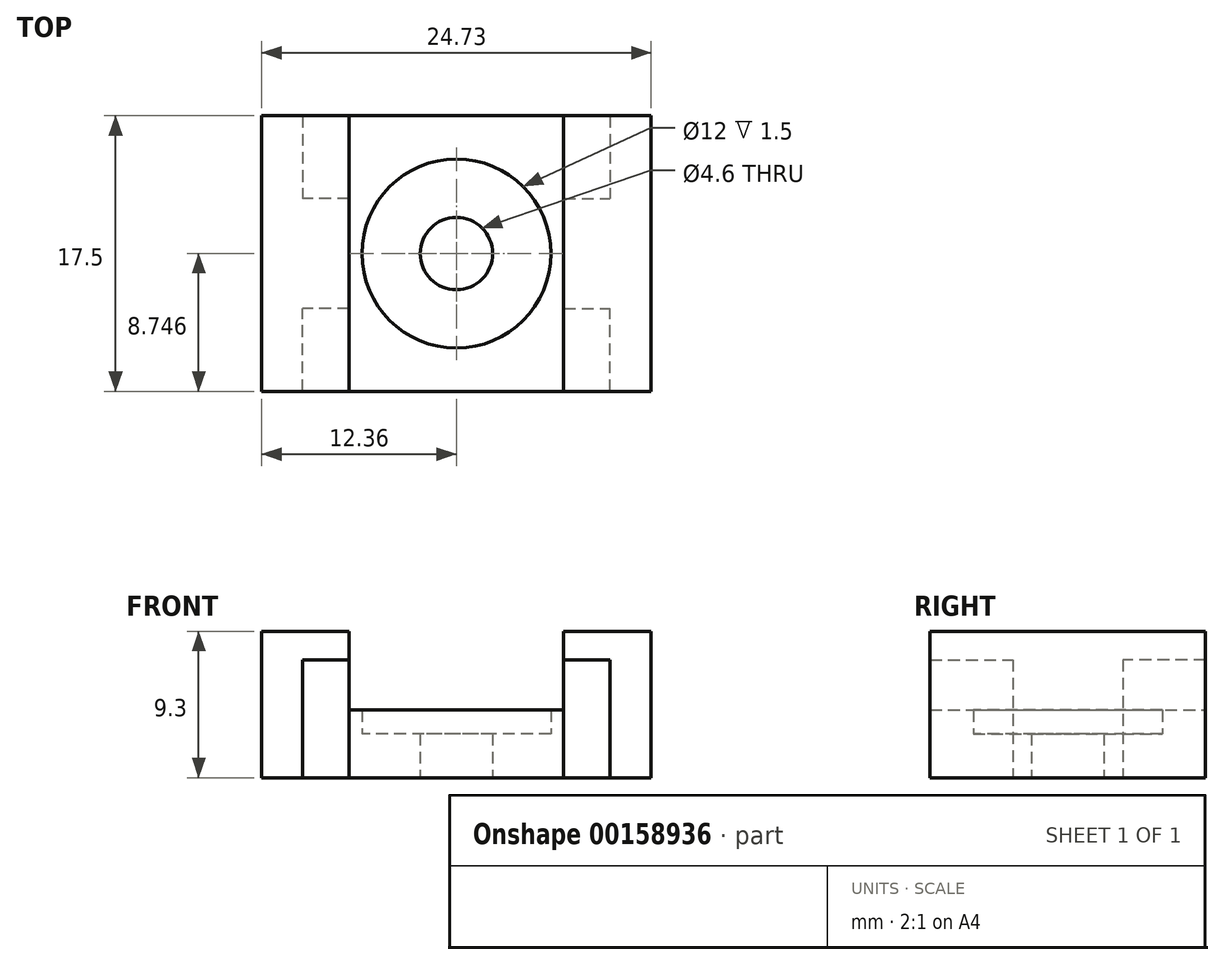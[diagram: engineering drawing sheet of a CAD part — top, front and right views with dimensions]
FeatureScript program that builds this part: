
annotation { "Feature Type Name" : "Feature", "Feature Type Description" : "" }
export const myFeature = defineFeature(function(context is Context, id is Id, definition is map)
    precondition{}
    {
        {
            var Q0;
            Q0=qCreatedBy(makeId("Top.planeOp"),FACE);
            var sketch = newSketch(context, id + "F0", { "sketchPlane" : qUnion([Q0])});
            skLineSegment(sketch, "E0.bottom", {"start": v(11.49, -0.86) * mm, "end": v(36.22, -0.86) * mm});
            skLineSegment(sketch, "E0.top", {"start": v(11.49, -18.36) * mm, "end": v(36.22, -18.36) * mm});
            skLineSegment(sketch, "E0.left", {"start": v(11.49, -0.86) * mm, "end": v(11.49, -18.36) * mm});
            skLineSegment(sketch, "E0.right", {"start": v(36.22, -0.86) * mm, "end": v(36.22, -18.36) * mm});
            skLineSegment(sketch, "E1", {"start": v(11.49, -18.36) * mm, "end": v(17.04, -18.36) * mm, "construction": true});
            skLineSegment(sketch, "E2", {"start": v(36.22, -18.36) * mm, "end": v(30.67, -18.36) * mm, "construction": true});
            skLineSegment(sketch, "E3", {"start": v(30.67, -18.36) * mm, "end": v(30.67, -0.86) * mm});
            skLineSegment(sketch, "E4", {"start": v(17.04, -18.36) * mm, "end": v(17.04, -0.86) * mm});
            skLineSegment(sketch, "E5", {"start": v(11.49, -9.61) * mm, "end": v(36.22, -9.61) * mm, "construction": true});
            skLineSegment(sketch, "E6", {"start": v(23.85, -0.86) * mm, "end": v(23.85, -18.36) * mm, "construction": true});
            skLineSegment(sketch, "E7", {"start": v(11.49, -13.1) * mm, "end": v(14.09, -13.1) * mm, "construction": true});
            skLineSegment(sketch, "E8", {"start": v(14.09, -13.1) * mm, "end": v(14.09, -18.36) * mm});
            skLineSegment(sketch, "E9", {"start": v(14.09, -13.1) * mm, "end": v(17.04, -13.1) * mm});
            skLineSegment(sketch, "E10.MirrorCS", {"start": v(33.62, -13.1) * mm, "end": v(30.67, -13.1) * mm});
            skLineSegment(sketch, "E11.MirrorCS", {"start": v(33.62, -13.1) * mm, "end": v(33.62, -18.36) * mm});
            skLineSegment(sketch, "E12.MirrorCS", {"start": v(33.62, -6.12) * mm, "end": v(30.67, -6.12) * mm});
            skLineSegment(sketch, "E13.MirrorCS", {"start": v(33.62, -6.12) * mm, "end": v(33.62, -0.86) * mm});
            skLineSegment(sketch, "E14.MirrorCS", {"start": v(14.09, -6.12) * mm, "end": v(17.04, -6.12) * mm});
            skLineSegment(sketch, "E15.MirrorCS", {"start": v(14.09, -6.12) * mm, "end": v(14.09, -0.86) * mm});
            skCircle(sketch, "E16", {"center": v(23.85, -9.61) * mm, "radius": 6 * mm});
            skCircle(sketch, "E17", {"center": v(23.85, -9.61) * mm, "radius": 2.3 * mm});
            skSolve(sketch);
        }
        {
            var Q0;
            {var subQ3=sQuery(id+"F0.wireOp",EDGE,"E0.right");Q0=makeQuery(id+"F0.imprint","IMPRINT",FACE,{"disambiguationData":[TD([[makeQuery(id+"F0.imprint","IMPRINT",EDGE,{"derivedFrom":subQ3}),-1.0]])]});}
            var Q1;
            {var subQ0=sQuery(id+"F0.wireOp",EDGE,"E0.left");Q1=makeQuery(id+"F0.imprint","IMPRINT",FACE,{"disambiguationData":[TD([[makeQuery(id+"F0.imprint","IMPRINT",EDGE,{"derivedFrom":subQ0}),1.0]])]});}
            extrude(context, id + "F1", {"entities" : qUnion([Q0, Q1]), "depth" : 9.3 * mm});
        }
        {
            var Q0;
            Q0=makeQuery(id+"F0.imprint","IMPRINT",FACE,{"disambiguationData":[TD([[makeQuery(id+"F0.imprint","IMPRINT",EDGE,{"derivedFrom":sQuery(id+"F0.wireOp",EDGE,"E16")}),-1.0]])]});
            extrude(context, id + "F2", {"entities" : qUnion([Q0]), "depth" : 4.3 * mm});
        }
        {
            var Q0;
            Q0=makeQuery(id+"F0.imprint","IMPRINT",FACE,{"disambiguationData":[TD([[makeQuery(id+"F0.imprint","IMPRINT",EDGE,{"derivedFrom":sQuery(id+"F0.wireOp",EDGE,"E16")}),1.0]])]});
            extrude(context, id + "F3", {"entities" : qUnion([Q0]), "operationType" : NewBodyOperationType.ADD, "depth" : 2.8 * mm});
        }
        {
            var Q0;
            Q0=makeQuery(id+"F1.opExtrude","SWEPT_FACE",FACE,{"disambiguationData":[OSD([sQuery(id+"F0.wireOp",EDGE,"E9")])]});
            var sketch = newSketch(context, id + "F4", { "sketchPlane" : qUnion([Q0])});
            skLineSegment(sketch, "E18.0.0", {"start": v(30.67, 0) * mm, "end": v(33.62, 0) * mm});
            skLineSegment(sketch, "E18.0.1", {"start": v(33.62, 0) * mm, "end": v(33.62, 9.3) * mm});
            skLineSegment(sketch, "E18.0.2", {"start": v(33.62, 9.3) * mm, "end": v(30.67, 9.3) * mm});
            skLineSegment(sketch, "E18.0.3", {"start": v(30.67, 9.3) * mm, "end": v(30.67, 0) * mm});
            skLineSegment(sketch, "E19.0.0", {"start": v(17.04, 0) * mm, "end": v(30.67, 0) * mm});
            skLineSegment(sketch, "E19.0.1", {"start": v(30.67, 0) * mm, "end": v(30.67, 4.3) * mm});
            skLineSegment(sketch, "E19.0.2", {"start": v(30.67, 4.3) * mm, "end": v(17.04, 4.3) * mm});
            skLineSegment(sketch, "E19.0.3", {"start": v(17.04, 4.3) * mm, "end": v(17.04, 0) * mm});
            skLineSegment(sketch, "E20", {"start": v(15.31, 7.5) * mm, "end": v(17.04, 7.5) * mm});
            skLineSegment(sketch, "E21", {"start": v(15.31, 7.5) * mm, "end": v(14.09, 7.5) * mm});
            skLineSegment(sketch, "E22", {"start": v(23.85, 0) * mm, "end": v(23.85, 4.3) * mm, "construction": true});
            skLineSegment(sketch, "E23.MirrorCS", {"start": v(32.39, 7.5) * mm, "end": v(33.62, 7.5) * mm});
            skLineSegment(sketch, "E24.MirrorCS", {"start": v(32.39, 7.5) * mm, "end": v(30.67, 7.5) * mm});
            skSolve(sketch);
        }
        {
            var Q0;
            {var subQ4=sQuery(id+"F4.wireOp",EDGE,"E20");Q0=makeQuery(id+"F4.imprint","IMPRINT",FACE,{"disambiguationData":[TD([[makeQuery(id+"F4.imprint","IMPRINT",EDGE,{"derivedFrom":subQ4}),1.0]])]});}
            extrude(context, id + "F5", {"entities" : qUnion([Q0]), "operationType" : NewBodyOperationType.ADD, "depth" : 5.26 * mm});
        }
        {
            var Q0;
            {var subQ2=sQuery(id+"F4.wireOp",EDGE,"E18.0.2");Q0=makeQuery(id+"F4.imprint","IMPRINT",FACE,{"disambiguationData":[TD([[makeQuery(id+"F4.imprint","IMPRINT",EDGE,{"derivedFrom":subQ2}),1.0]])]});}
            extrude(context, id + "F6", {"entities" : qUnion([Q0]), "operationType" : NewBodyOperationType.ADD, "depth" : 5.26 * mm});
        }
        {
            var Q0;
            Q0=makeQuery(id+"F1.opExtrude","SWEPT_FACE",FACE,{"disambiguationData":[OSD([sQuery(id+"F0.wireOp",EDGE,"E12.MirrorCS")])]});
            var sketch = newSketch(context, id + "F7", { "sketchPlane" : qUnion([Q0])});
            skLineSegment(sketch, "E25.0.0", {"start": v(-17.04, 0) * mm, "end": v(-14.09, 0) * mm});
            skLineSegment(sketch, "E25.0.1", {"start": v(-14.09, 0) * mm, "end": v(-14.09, 9.3) * mm});
            skLineSegment(sketch, "E25.0.2", {"start": v(-14.09, 9.3) * mm, "end": v(-17.04, 9.3) * mm});
            skLineSegment(sketch, "E25.0.3", {"start": v(-17.04, 9.3) * mm, "end": v(-17.04, 0) * mm});
            skLineSegment(sketch, "E26", {"start": v(-32.14, 9.3) * mm, "end": v(-32.14, 7.5) * mm, "construction": true});
            skLineSegment(sketch, "E27", {"start": v(-32.14, 7.5) * mm, "end": v(-30.67, 7.5) * mm});
            skLineSegment(sketch, "E28", {"start": v(-32.14, 7.5) * mm, "end": v(-33.62, 7.5) * mm});
            skLineSegment(sketch, "E29.0.0", {"start": v(-30.67, 0) * mm, "end": v(-17.04, 0) * mm});
            skLineSegment(sketch, "E29.0.1", {"start": v(-17.04, 0) * mm, "end": v(-17.04, 4.3) * mm});
            skLineSegment(sketch, "E29.0.2", {"start": v(-17.04, 4.3) * mm, "end": v(-30.67, 4.3) * mm});
            skLineSegment(sketch, "E29.0.3", {"start": v(-30.67, 4.3) * mm, "end": v(-30.67, 0) * mm});
            skLineSegment(sketch, "E30", {"start": v(-23.85, 4.3) * mm, "end": v(-23.85, 0) * mm, "construction": true});
            skLineSegment(sketch, "E31.MirrorCS", {"start": v(-15.56, 7.5) * mm, "end": v(-17.04, 7.5) * mm});
            skLineSegment(sketch, "E32.MirrorCS", {"start": v(-15.56, 7.5) * mm, "end": v(-14.09, 7.5) * mm});
            skSolve(sketch);
        }
        {
            var Q0;
            {var subQ4=sQuery(id+"F7.wireOp",EDGE,"E27");Q0=makeQuery(id+"F7.imprint","IMPRINT",FACE,{"disambiguationData":[TD([[makeQuery(id+"F7.imprint","IMPRINT",EDGE,{"derivedFrom":subQ4}),1.0]])]});}
            extrude(context, id + "F8", {"entities" : qUnion([Q0]), "operationType" : NewBodyOperationType.ADD, "depth" : 5.26 * mm});
        }
        {
            var Q0;
            {var subQ2=sQuery(id+"F7.wireOp",EDGE,"E25.0.2");Q0=makeQuery(id+"F7.imprint","IMPRINT",FACE,{"disambiguationData":[TD([[makeQuery(id+"F7.imprint","IMPRINT",EDGE,{"derivedFrom":subQ2}),1.0]])]});}
            extrude(context, id + "F9", {"entities" : qUnion([Q0]), "operationType" : NewBodyOperationType.ADD, "depth" : 5.26 * mm});
        }
    });
